# Revit family: ShowerColumn-RiserRailKitwithHandShower-HoseAndOutlet-Vitra-A45743
name_source: partatom
category: Plumbing Fixtures
revit_build: Autodesk Revit 2017 (Build: 20160225_1515(x64)
units: mm (PartAtom-declared; Revit-internal decimal feet)

## family parameters
Cut with Voids When Loaded = No
Host = Face
OmniClass Number = 23.45.55.17
OmniClass Title = Mixing Faucets
Part Type = Normal
Room Calculation Point = No
Round Connector Dimension = Use Diameter
Shared = Yes

## types (1)
- ShowerColumn-RiserRailKitwithHandShower-HoseAndOutlet-Vitra-A45743
    Article No. (default) = A45743
    BIMobject category = Bath/Shower Mixer
    Brand = VitrA
    CW Connection = Yes
    CWFU = 0
    Coating Material = Chrome (Metal)
    Color = Chrome
    Connection Diameter (mm) = 15 mm  [stored 0.0492126 ft]
    Cost = 0 $
    Default Elevation = 0 mm  [stored 0 ft]
    Depth(mm) = 290 mm  [stored 0.951444 ft]
    Description = ShowerColumn-RiserRailKitwithHandShower-HoseAndOutlet-Vitra
    Design country = Turkey
    HW Connection = Yes
    HWFU = 0
    Height(mm) = 900 mm  [stored 2.95276 ft]
    IFC Classification = Sanitary Terminal
    Manufacturer = Vitra
    Manufacturer name = Vitra
    Masterformat 2014 Code = 22 41 23
    Masterformat 2014 Description = Residential Showers
    Model = A45743
    MountingType = Wall-mounted
    NBS Referans Code = 35-06-81
    NBS Referans Description = Shower Heads
    Number Of Connections = 1 mm  [stored 0.00328084 ft]
    OmniClass Code = 23-31 17 19
    OmniClass Description = Shower Head Fixtures
    Product SKU = A45743
    Product Type = Showerhead Set
    Product certification = https://www.vitraglobal.com
    Product family = Shower System
    Product group = ShowerSet
    Product url = https://vitraglobal.com
    Range of flow pressure = 0.5-10 bar (Recommended 3-5 Bars)
    Technical description = https://vitraglobal.com
    UNSPSC Code = 30181503
    URL = https://vitraglobal.com
    Uniclass 1.4 Code = L7214
    Uniclass 1.4 Description = Showers
    Uniclass 2.0 Code = PR-35-06-81
    Uniclass 2.0 Description = Shower Heads
    Uniclass 2015 Code = Pr_40_20_87_76
    Uniclass 2015 Name = Shower heads
    Uniformat II Code = D2010
    Uniformat II Description = Plumbing Fixtures
    Vent Connection = No
    WFU = 0
    Warranty Period (Year) = 5 Years
    Waste Connection = No
    Width(mm) = 260 mm  [stored 0.853018 ft]
    Youtube = https://www.youtube.com

note: [stored X ft] marks values corroborated as IEEE doubles in the binary element streams (Revit-internal decimal feet)

## geometry (parser evidence)
native form markers: Sweep x2
no freeform markers — native parametric forms only
